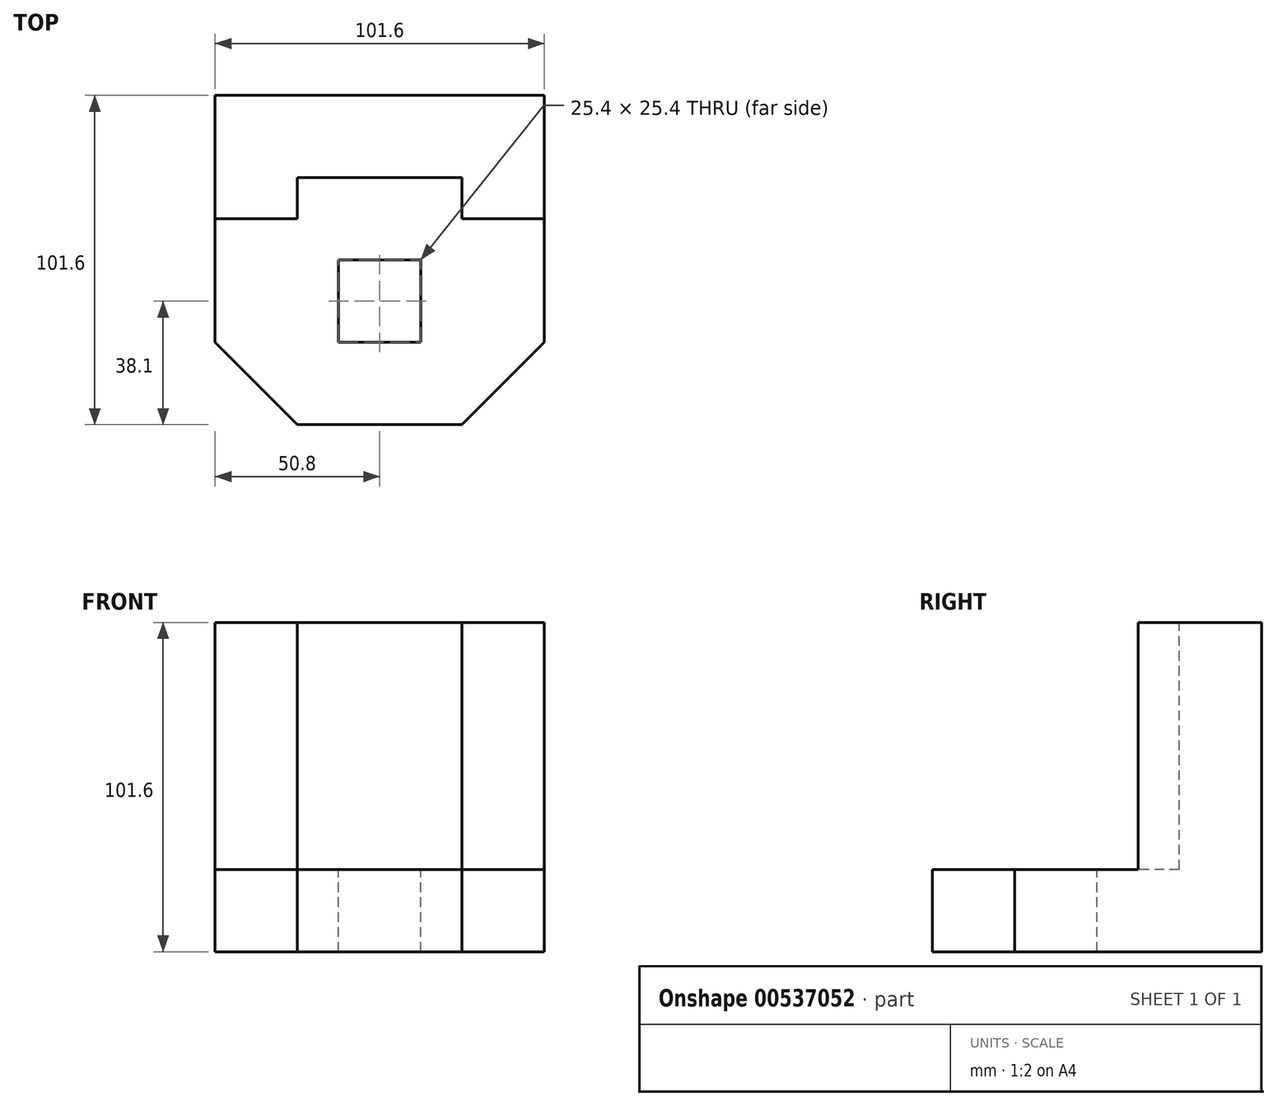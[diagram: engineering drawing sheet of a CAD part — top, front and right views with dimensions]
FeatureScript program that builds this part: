
annotation { "Feature Type Name" : "Feature", "Feature Type Description" : "" }
export const myFeature = defineFeature(function(context is Context, id is Id, definition is map)
    precondition{}
    {
        {
            var Q0;
            Q0=qCreatedBy(makeId("Top.planeOp"),FACE);
            var sketch = newSketch(context, id + "F0", { "sketchPlane" : qUnion([Q0])});
            skLineSegment(sketch, "E0.bottom", {"start": v(0, 0) * mm, "end": v(-101.6, 0) * mm});
            skLineSegment(sketch, "E0.top", {"start": v(0, -101.6) * mm, "end": v(-101.6, -101.6) * mm});
            skLineSegment(sketch, "E0.left", {"start": v(0, 0) * mm, "end": v(0, -101.6) * mm});
            skLineSegment(sketch, "E0.right", {"start": v(-101.6, 0) * mm, "end": v(-101.6, -101.6) * mm});
            skSolve(sketch);
        }
        {
            var Q0;
            Q0=makeQuery(id+"F0.imprint","IMPRINT",FACE,{"disambiguationData":[TD([[makeQuery(id+"F0.imprint","IMPRINT",EDGE,{"derivedFrom":sQuery(id+"F0.wireOp",EDGE,"E0.bottom")}),1.0]])]});
            extrude(context, id + "F1", {"entities" : qUnion([Q0]), "depth" : 101.6 * mm, "offsetDistance" : 25.4 * mm});
        }
        {
            var Q0;
            Q0=makeQuery(id+"F1.opExtrude","SWEPT_FACE",FACE,{"disambiguationData":[OSD([sQuery(id+"F0.wireOp",EDGE,"E0.left")])]});
            var sketch = newSketch(context, id + "F2", { "sketchPlane" : qUnion([Q0])});
            skLineSegment(sketch, "E1", {"start": v(-101.6, 0) * mm, "end": v(-101.6, 25.4) * mm});
            skLineSegment(sketch, "E2", {"start": v(-101.6, 25.4) * mm, "end": v(-38.1, 25.4) * mm});
            skLineSegment(sketch, "E3", {"start": v(-38.1, 25.4) * mm, "end": v(-38.1, 101.6) * mm});
            skSolve(sketch);
        }
        {
            var Q0;
            {var subQ0=sQuery(id+"F2.wireOp",EDGE,"E2");Q0=makeQuery(id+"F2.imprint","IMPRINT",FACE,{"disambiguationData":[TD([[makeQuery(id+"F2.imprint","IMPRINT",EDGE,{"derivedFrom":subQ0}),1.0]])]});}
            extrude(context, id + "F3", {"entities" : qUnion([Q0]), "operationType" : NewBodyOperationType.REMOVE, "oppositeDirection" : true, "depth" : 109.73 * mm, "offsetDistance" : 25.4 * mm});
        }
        {
            var Q0;
            Q0=makeQuery(id+"F3.boolean.opBoolean","COPY",FACE,{"derivedFrom":makeQuery(id+"F3.opExtrude","SWEPT_FACE",FACE,{"disambiguationData":[OSD([sQuery(id+"F2.wireOp",EDGE,"E2")])]})});
            var sketch = newSketch(context, id + "F4", { "sketchPlane" : qUnion([Q0])});
            skLineSegment(sketch, "E4", {"start": v(-101.6, -101.6) * mm, "end": v(-101.6, -76.2) * mm});
            skLineSegment(sketch, "E5", {"start": v(-101.6, -76.2) * mm, "end": v(-76.2, -101.6) * mm});
            skLineSegment(sketch, "E6", {"start": v(-76.2, -101.6) * mm, "end": v(-101.6, -101.6) * mm});
            skLineSegment(sketch, "E7", {"start": v(0, -101.6) * mm, "end": v(0, -76.2) * mm});
            skLineSegment(sketch, "E8", {"start": v(0, -76.2) * mm, "end": v(-25.4, -101.6) * mm});
            skLineSegment(sketch, "E9", {"start": v(-25.4, -101.6) * mm, "end": v(0, -101.6) * mm});
            skLineSegment(sketch, "E10", {"start": v(-101.6, -76.2) * mm, "end": v(-63.5, -76.2) * mm});
            skLineSegment(sketch, "E11", {"start": v(-63.5, -76.2) * mm, "end": v(-63.5, -50.8) * mm});
            skLineSegment(sketch, "E12", {"start": v(-63.5, -50.8) * mm, "end": v(-38.1, -50.8) * mm});
            skLineSegment(sketch, "E13", {"start": v(-38.1, -50.8) * mm, "end": v(-38.1, -76.2) * mm});
            skLineSegment(sketch, "E14", {"start": v(-38.1, -76.2) * mm, "end": v(-63.5, -76.2) * mm});
            skLineSegment(sketch, "E15", {"start": v(-38.1, -76.2) * mm, "end": v(0, -76.2) * mm});
            skSolve(sketch);
        }
        {
            var Q0;
            Q0=makeQuery(id+"F4.imprint","IMPRINT",FACE,{"disambiguationData":[TD([[makeQuery(id+"F4.imprint","IMPRINT",EDGE,{"derivedFrom":sQuery(id+"F4.wireOp",EDGE,"E7")}),1.0]])]});
            var Q1;
            Q1=makeQuery(id+"F4.imprint","IMPRINT",FACE,{"disambiguationData":[TD([[makeQuery(id+"F4.imprint","IMPRINT",EDGE,{"derivedFrom":sQuery(id+"F4.wireOp",EDGE,"E4")}),-1.0]])]});
            var Q2;
            Q2=makeQuery(id+"F4.imprint","IMPRINT",FACE,{"disambiguationData":[TD([[makeQuery(id+"F4.imprint","IMPRINT",EDGE,{"derivedFrom":sQuery(id+"F4.wireOp",EDGE,"E11")}),-1.0]])]});
            extrude(context, id + "F5", {"entities" : qUnion([Q0, Q1, Q2]), "operationType" : NewBodyOperationType.REMOVE, "oppositeDirection" : true, "depth" : 70.87 * mm, "offsetDistance" : 25.4 * mm});
        }
        {
            var Q0;
            Q0=makeQuery(id+"F1.opExtrude","CAP_FACE",FACE,{"disambiguationData":[OSD([sQuery(id+"F0.wireOp",EDGE,"E0.bottom"),sQuery(id+"F0.wireOp",EDGE,"E0.top"),sQuery(id+"F0.wireOp",EDGE,"E0.left"),sQuery(id+"F0.wireOp",EDGE,"E0.right")])],"isStart":false});
            var sketch = newSketch(context, id + "F6", { "sketchPlane" : qUnion([Q0])});
            skLineSegment(sketch, "E16", {"start": v(-101.6, -38.1) * mm, "end": v(-76.2, -38.1) * mm});
            skLineSegment(sketch, "E17", {"start": v(-76.2, -38.1) * mm, "end": v(-76.2, -25.4) * mm});
            skLineSegment(sketch, "E18", {"start": v(-76.2, -25.4) * mm, "end": v(-25.4, -25.4) * mm});
            skLineSegment(sketch, "E19", {"start": v(-25.4, -25.4) * mm, "end": v(-25.4, -38.1) * mm});
            skSolve(sketch);
        }
        {
            var Q0;
            {var subQ0=sQuery(id+"F6.wireOp",EDGE,"E17");Q0=makeQuery(id+"F6.imprint","IMPRINT",FACE,{"disambiguationData":[TD([[makeQuery(id+"F6.imprint","IMPRINT",EDGE,{"derivedFrom":subQ0}),-1.0]])]});}
            extrude(context, id + "F7", {"entities" : qUnion([Q0]), "operationType" : NewBodyOperationType.REMOVE, "oppositeDirection" : true, "depth" : 76.2 * mm, "offsetDistance" : 25.4 * mm});
        }
    });
